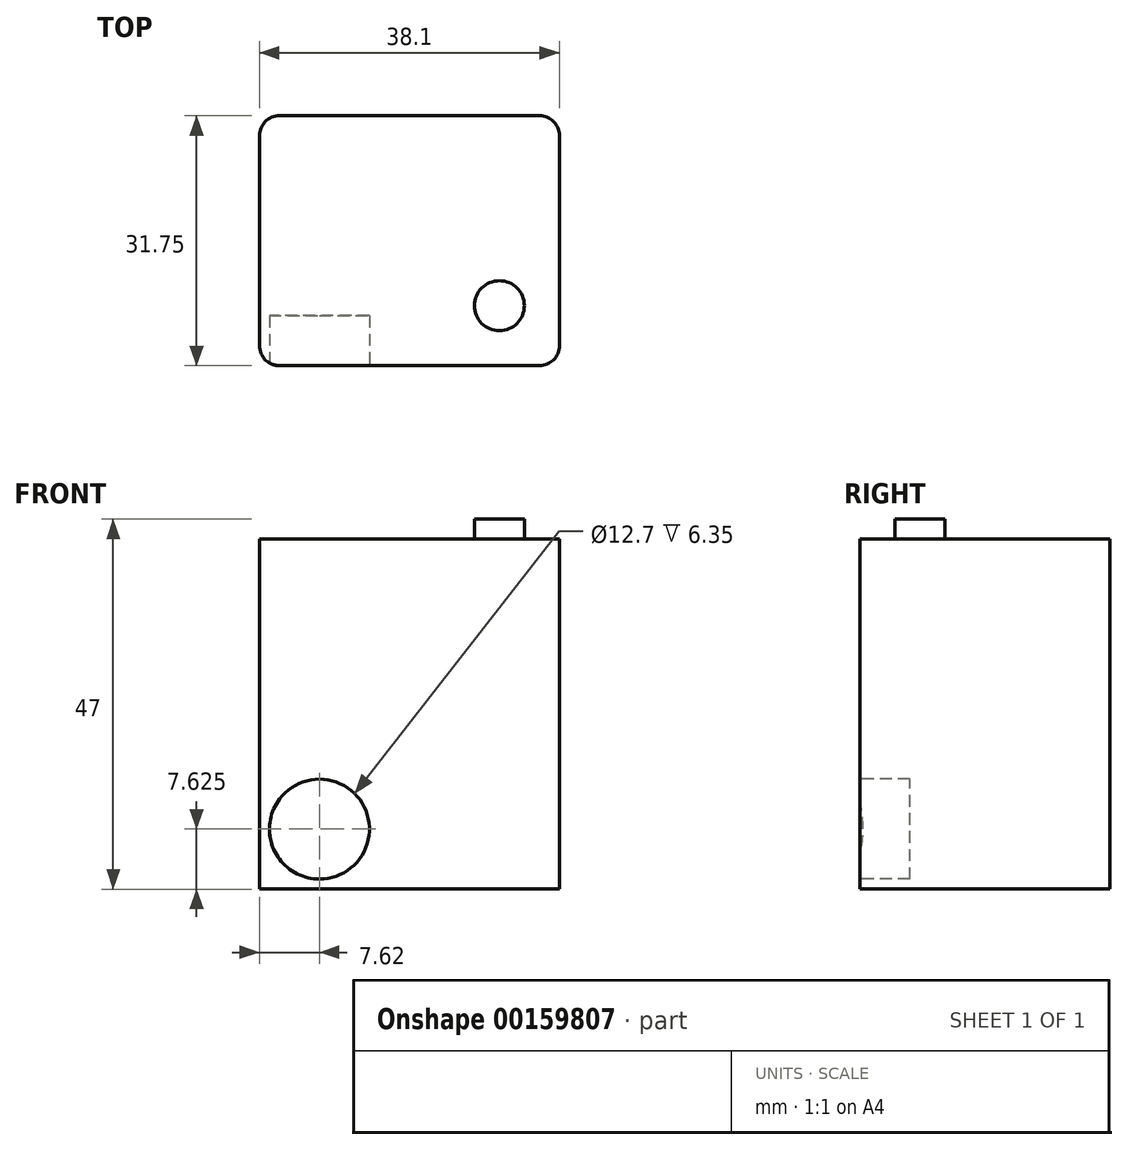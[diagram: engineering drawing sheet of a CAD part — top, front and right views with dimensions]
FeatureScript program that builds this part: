
annotation { "Feature Type Name" : "Feature", "Feature Type Description" : "" }
export const myFeature = defineFeature(function(context is Context, id is Id, definition is map)
    precondition{}
    {
        {
            var Q0;
            Q0=qCreatedBy(makeId("Front.planeOp"),FACE);
            var sketch = newSketch(context, id + "F0", { "sketchPlane" : qUnion([Q0])});
            skLineSegment(sketch, "E0.bottom", {"start": v(-19.05, 22.23) * mm, "end": v(19.05, 22.23) * mm});
            skLineSegment(sketch, "E0.top", {"start": v(-19.05, -22.23) * mm, "end": v(19.05, -22.23) * mm});
            skLineSegment(sketch, "E0.left", {"start": v(-19.05, 22.23) * mm, "end": v(-19.05, -22.23) * mm});
            skLineSegment(sketch, "E0.right", {"start": v(19.05, 22.23) * mm, "end": v(19.05, -22.23) * mm});
            skPoint(sketch, "E0.middle", {"position": v(0, 0) * mm});
            skSolve(sketch);
        }
        {
            var Q0;
            Q0 = qSketchRegion(id + "F0", true);
            extrude(context, id + "F1", {"entities" : qUnion([Q0]), "depth" : 31.75 * mm});
        }
        {
            var Q0;
            Q0=makeQuery(id+"F1.opExtrude","CAP_FACE",FACE,{"disambiguationData":[OSD([sQuery(id+"F0.wireOp",EDGE,"E0.bottom"),sQuery(id+"F0.wireOp",EDGE,"E0.top"),sQuery(id+"F0.wireOp",EDGE,"E0.left"),sQuery(id+"F0.wireOp",EDGE,"E0.right")])],"isStart":false});
            var sketch = newSketch(context, id + "F2", { "sketchPlane" : qUnion([Q0])});
            skCircle(sketch, "E1", {"center": v(-11.43, -14.6) * mm, "radius": 6.35 * mm});
            skSolve(sketch);
        }
        {
            var Q0;
            Q0 = qSketchRegion(id + "F2", true);
            extrude(context, id + "F3", {"entities" : qUnion([Q0]), "operationType" : NewBodyOperationType.REMOVE, "oppositeDirection" : true, "depth" : 6.35 * mm});
        }
        {
            var Q0;
            Q0=makeQuery(id+"F1.opExtrude","SWEPT_FACE",FACE,{"disambiguationData":[OSD([sQuery(id+"F0.wireOp",EDGE,"E0.bottom")])]});
            var sketch = newSketch(context, id + "F4", { "sketchPlane" : qUnion([Q0])});
            skCircle(sketch, "E2", {"center": v(11.43, -24.13) * mm, "radius": 3.18 * mm});
            skSolve(sketch);
        }
        {
            var Q0;
            Q0 = qSketchRegion(id + "F4", true);
            extrude(context, id + "F5", {"entities" : qUnion([Q0]), "operationType" : NewBodyOperationType.ADD, "depth" : 2.54 * mm});
        }
        {
            var Q0;
            Q0=makeQuery(id+"F1.opExtrude","CAP_EDGE",EDGE,{"disambiguationData":[OSD([sQuery(id+"F0.wireOp",EDGE,"E0.left")])],"isStart":false});
            var Q1;
            Q1=makeQuery(id+"F1.opExtrude","CAP_EDGE",EDGE,{"disambiguationData":[OSD([sQuery(id+"F0.wireOp",EDGE,"E0.right")])],"isStart":false});
            var Q2;
            Q2=makeQuery(id+"F1.opExtrude","CAP_EDGE",EDGE,{"disambiguationData":[OSD([sQuery(id+"F0.wireOp",EDGE,"E0.left")])],"isStart":true});
            var Q3;
            Q3=makeQuery(id+"F1.opExtrude","CAP_EDGE",EDGE,{"disambiguationData":[OSD([sQuery(id+"F0.wireOp",EDGE,"E0.right")])],"isStart":true});
            fillet(context, id + "F6", {"entities" : qUnion([Q0, Q1, Q2, Q3]), "radius" : 2.54 * mm, "tangentPropagation" : true, "allowEdgeOverflow" : false});
        }
    });
